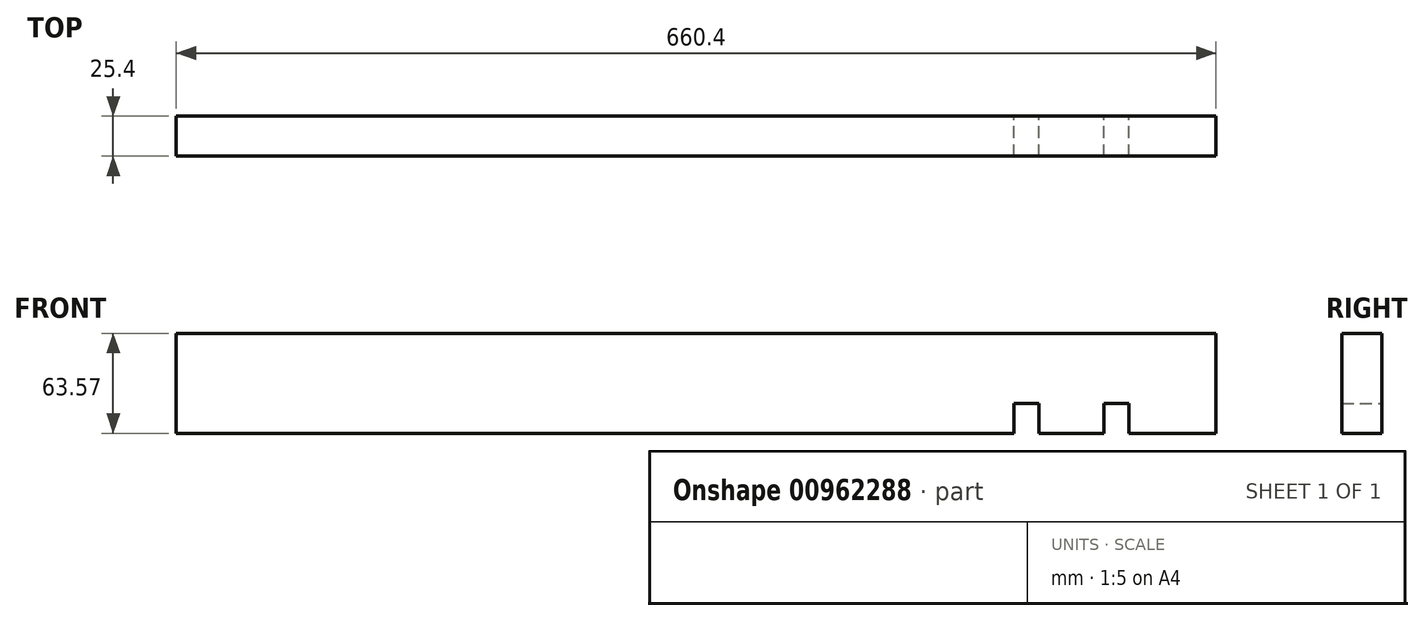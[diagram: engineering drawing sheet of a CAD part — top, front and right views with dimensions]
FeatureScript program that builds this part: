
annotation { "Feature Type Name" : "Feature", "Feature Type Description" : "" }
export const myFeature = defineFeature(function(context is Context, id is Id, definition is map)
    precondition{}
    {
        {
            var Q0;
            Q0=qCreatedBy(makeId("Front.planeOp"),FACE);
            var sketch = newSketch(context, id + "F0", { "sketchPlane" : qUnion([Q0])});
            skLineSegment(sketch, "E0", {"start": v(-203.73, 0) * mm, "end": v(-203.73, 63.57) * mm});
            skLineSegment(sketch, "E1", {"start": v(-203.73, 63.57) * mm, "end": v(456.67, 63.57) * mm});
            skLineSegment(sketch, "E2", {"start": v(456.67, 63.57) * mm, "end": v(456.67, 0) * mm});
            skLineSegment(sketch, "E3", {"start": v(456.67, 0) * mm, "end": v(401.3, 0) * mm});
            skLineSegment(sketch, "E4", {"start": v(401.3, 0) * mm, "end": v(401.3, 19.05) * mm});
            skLineSegment(sketch, "E5", {"start": v(401.3, 19.05) * mm, "end": v(385.42, 19.05) * mm});
            skLineSegment(sketch, "E6", {"start": v(385.42, 19.05) * mm, "end": v(385.42, 0) * mm});
            skLineSegment(sketch, "E7", {"start": v(385.42, 0) * mm, "end": v(344.15, 0) * mm});
            skLineSegment(sketch, "E8", {"start": v(344.15, 0) * mm, "end": v(344.15, 19.05) * mm});
            skLineSegment(sketch, "E9", {"start": v(344.15, 19.05) * mm, "end": v(328.27, 19.05) * mm});
            skLineSegment(sketch, "E10", {"start": v(328.27, 19.05) * mm, "end": v(328.27, 0) * mm});
            skPoint(sketch, "E11", {"position": v(336.21, 19.05) * mm});
            skPoint(sketch, "E12", {"position": v(393.36, 19.05) * mm});
            skLineSegment(sketch, "E13", {"start": v(-203.73, 0) * mm, "end": v(328.27, 0) * mm});
            skSolve(sketch);
        }
        {
            var Q0;
            Q0=makeQuery(id+"F0.imprint","IMPRINT",FACE,{"disambiguationData":[TD([[makeQuery(id+"F0.imprint","IMPRINT",EDGE,{"derivedFrom":sQuery(id+"F0.wireOp",EDGE,"E0")}),-1.0]])]});
            extrude(context, id + "F1", {"entities" : qUnion([Q0]), "depth" : 25.4 * mm, "offsetDistance" : 25.4 * mm});
        }
    });
